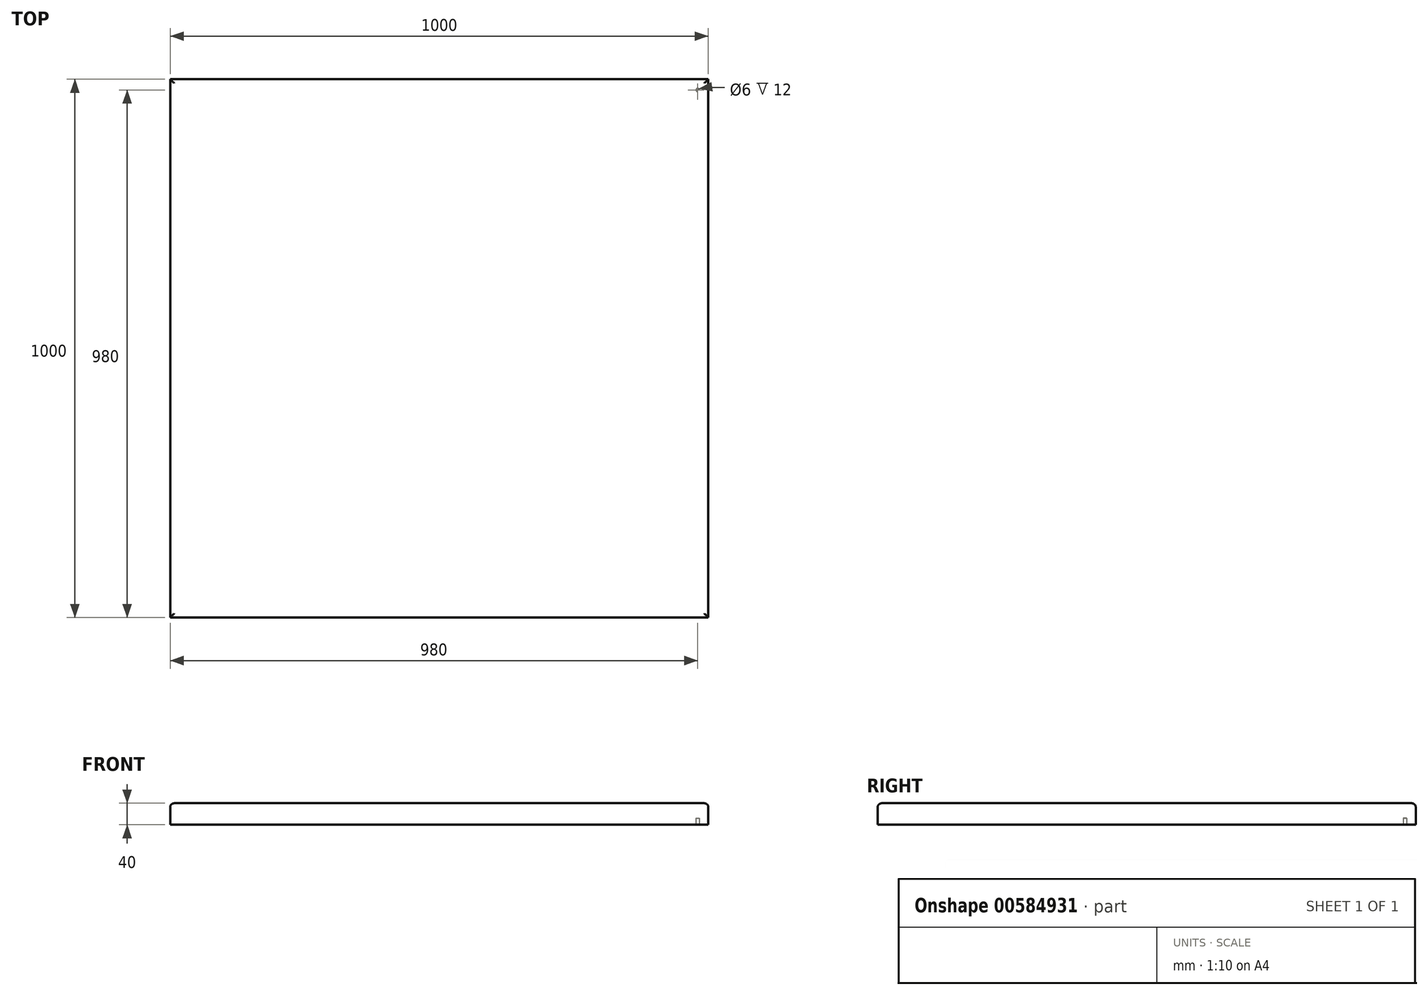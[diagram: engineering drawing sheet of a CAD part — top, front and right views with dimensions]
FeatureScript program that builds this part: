
annotation { "Feature Type Name" : "Feature", "Feature Type Description" : "" }
export const myFeature = defineFeature(function(context is Context, id is Id, definition is map)
    precondition{}
    {
        {
            var Q0;
            Q0=qCreatedBy(makeId("Front.planeOp"),FACE);
            var sketch = newSketch(context, id + "F0", { "sketchPlane" : qUnion([Q0])});
            skLineSegment(sketch, "E0.bottom", {"start": v(0, 0) * mm, "end": v(1000, 0) * mm});
            skLineSegment(sketch, "E0.top", {"start": v(0, 40) * mm, "end": v(1000, 40) * mm});
            skLineSegment(sketch, "E0.left", {"start": v(0, 0) * mm, "end": v(0, 40) * mm});
            skLineSegment(sketch, "E0.right", {"start": v(1000, 0) * mm, "end": v(1000, 40) * mm});
            skSolve(sketch);
        }
        {
            var Q0;
            Q0=makeQuery(id+"F0.imprint","IMPRINT",FACE,{"disambiguationData":[TD([[makeQuery(id+"F0.imprint","IMPRINT",EDGE,{"derivedFrom":sQuery(id+"F0.wireOp",EDGE,"E0.bottom")}),1.0]])]});
            extrude(context, id + "F1", {"entities" : qUnion([Q0]), "depth" : 1000 * mm, "offsetDistance" : 25 * mm});
        }
        {
            var Q0;
            Q0=makeQuery(id+"F1.opExtrude","SWEPT_FACE",FACE,{"disambiguationData":[OSD([sQuery(id+"F0.wireOp",EDGE,"E0.top")])]});
            fillet(context, id + "F2", {"entities" : qUnion([Q0]), "radius" : 7.5 * mm, "tangentPropagation" : true, "allowEdgeOverflow" : false});
        }
        {
            var Q0;
            Q0=makeQuery(id+"F1.opExtrude","SWEPT_FACE",FACE,{"disambiguationData":[OSD([sQuery(id+"F0.wireOp",EDGE,"E0.bottom")])]});
            var sketch = newSketch(context, id + "F3", { "sketchPlane" : qUnion([Q0])});
            skCircle(sketch, "E1", {"center": v(980, 20) * mm, "radius": 3 * mm});
            skSolve(sketch);
        }
        {
            var Q0;
            Q0=makeQuery(id+"F3.imprint","IMPRINT",FACE,{"disambiguationData":[TD([[makeQuery(id+"F3.imprint","IMPRINT",EDGE,{"derivedFrom":sQuery(id+"F3.wireOp",EDGE,"E1")}),1.0]])]});
            extrude(context, id + "F4", {"entities" : qUnion([Q0]), "operationType" : NewBodyOperationType.REMOVE, "oppositeDirection" : true, "depth" : 12 * mm, "offsetDistance" : 25 * mm});
        }
    });
